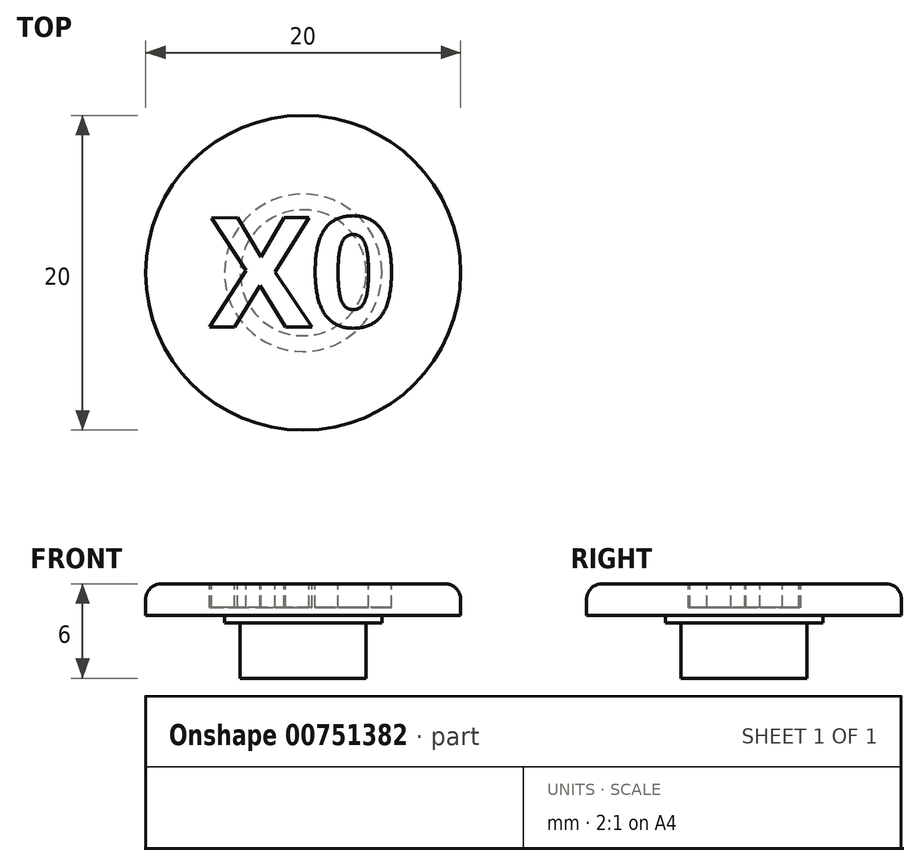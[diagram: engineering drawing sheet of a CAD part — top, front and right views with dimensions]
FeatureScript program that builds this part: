
annotation { "Feature Type Name" : "Feature", "Feature Type Description" : "" }
export const myFeature = defineFeature(function(context is Context, id is Id, definition is map)
    precondition{}
    {
        {
            var Q0;
            Q0=qCreatedBy(makeId("Top.planeOp"),FACE);
            var sketch = newSketch(context, id + "F0", { "sketchPlane" : qUnion([Q0])});
            skCircle(sketch, "E0", {"center": v(0, 0) * mm, "radius": 10 * mm});
            skCircle(sketch, "E1", {"center": v(0, 0) * mm, "radius": 4 * mm});
            skCircle(sketch, "E2", {"center": v(0, 0) * mm, "radius": 5 * mm});
            skSolve(sketch);
        }
        {
            var Q0;
            Q0=makeQuery(id+"F0.imprint","IMPRINT",FACE,{"disambiguationData":[TD([[makeQuery(id+"F0.imprint","IMPRINT",EDGE,{"derivedFrom":sQuery(id+"F0.wireOp",EDGE,"E1")}),1.0]])]});
            extrude(context, id + "F1", {"entities" : qUnion([Q0]), "oppositeDirection" : true, "depth" : 6 * mm, "offsetDistance" : 25 * mm});
        }
        {
            var Q0;
            Q0=makeQuery(id+"F0.imprint","IMPRINT",FACE,{"disambiguationData":[TD([[makeQuery(id+"F0.imprint","IMPRINT",EDGE,{"derivedFrom":sQuery(id+"F0.wireOp",EDGE,"E1")}),-1.0]])]});
            extrude(context, id + "F2", {"entities" : qUnion([Q0]), "operationType" : NewBodyOperationType.ADD, "oppositeDirection" : true, "depth" : 2.5 * mm, "offsetDistance" : 25 * mm});
        }
        {
            var Q0;
            Q0=makeQuery(id+"F0.imprint","IMPRINT",FACE,{"disambiguationData":[TD([[makeQuery(id+"F0.imprint","IMPRINT",EDGE,{"derivedFrom":sQuery(id+"F0.wireOp",EDGE,"E0")}),1.0]])]});
            extrude(context, id + "F3", {"entities" : qUnion([Q0]), "operationType" : NewBodyOperationType.ADD, "oppositeDirection" : true, "depth" : 2 * mm, "offsetDistance" : 25 * mm});
        }
        {
            var Q0;
            Q0=makeQuery(id+"F3.opExtrude","CAP_EDGE",EDGE,{"disambiguationData":[OSD([sQuery(id+"F0.wireOp",EDGE,"E0")])],"isStart":true});
            fillet(context, id + "F4", {"entities" : qUnion([Q0]), "radius" : 1 * mm, "tangentPropagation" : true, "allowEdgeOverflow" : false});
        }
        {
            var Q0;
            Q0=qCreatedBy(makeId("Top.planeOp"),FACE);
            var sketch = newSketch(context, id + "F5", { "sketchPlane" : qUnion([Q0])});
            skText(sketch, "E3", { "text": "X", "fontName": "OpenSans-Bold.ttf"});
            skText(sketch, "E4", { "text": "0", "fontName": "OpenSans-Bold.ttf"});
            skPoint(sketch, "E5", {"position": v(0.41, 0.07) * mm});
            skPoint(sketch, "E6", {"position": v(1.18, 0.07) * mm});
            const initialGuessF5  = {"E3": [-0.00593, -0.00345, 1, 0.0028, 0.007], "E4": [0.00041, -0.00343, 1, 0, 0.007]};
            skSetInitialGuess(sketch, initialGuessF5);
            skSolve(sketch);
        }
        {
            var Q0;
            Q0=makeQuery(id+"F5.imprint","IMPRINT",FACE,{"disambiguationData":[TD([[makeQuery(id+"F5.imprint","IMPRINT",EDGE,{"derivedFrom":sQuery(id+"F5.wireOp",EDGE,"E3.sketch_text.stroke-0")}),-1.0]])]});
            var Q1;
            Q1=makeQuery(id+"F5.imprint","IMPRINT",FACE,{"disambiguationData":[TD([[makeQuery(id+"F5.imprint","IMPRINT",EDGE,{"derivedFrom":sQuery(id+"F5.wireOp",EDGE,"E4.sketch_text.stroke-0")}),-1.0]])]});
            extrude(context, id + "F6", {"entities" : qUnion([Q0, Q1]), "operationType" : NewBodyOperationType.REMOVE, "oppositeDirection" : true, "depth" : 1.5 * mm, "offsetDistance" : 25 * mm});
        }
    });
